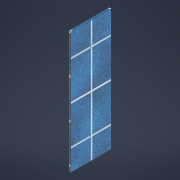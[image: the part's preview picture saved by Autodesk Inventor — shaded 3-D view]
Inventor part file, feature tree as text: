
AUTODESK INVENTOR PART (.ipt)
format: ipt  version: 2022 (Build 260153000, 153)  size: 121,856 bytes
history: native  units: mm
features: extrude x1, sketch x1
ambient origin geometry x8: Origin, YZ Plane, XZ Plane, XY Plane, X Axis, Y Axis, Z Axis, Center Point
bodies: Solid1 (feature_tree)
feature tree (2):
  extrude  "Extrusion1"  Depth=40.0mm
  sketch  "Sketch1"  dims[d0=120.0mm d1=40.0mm d2=2.0mm d3=0.0mm]
